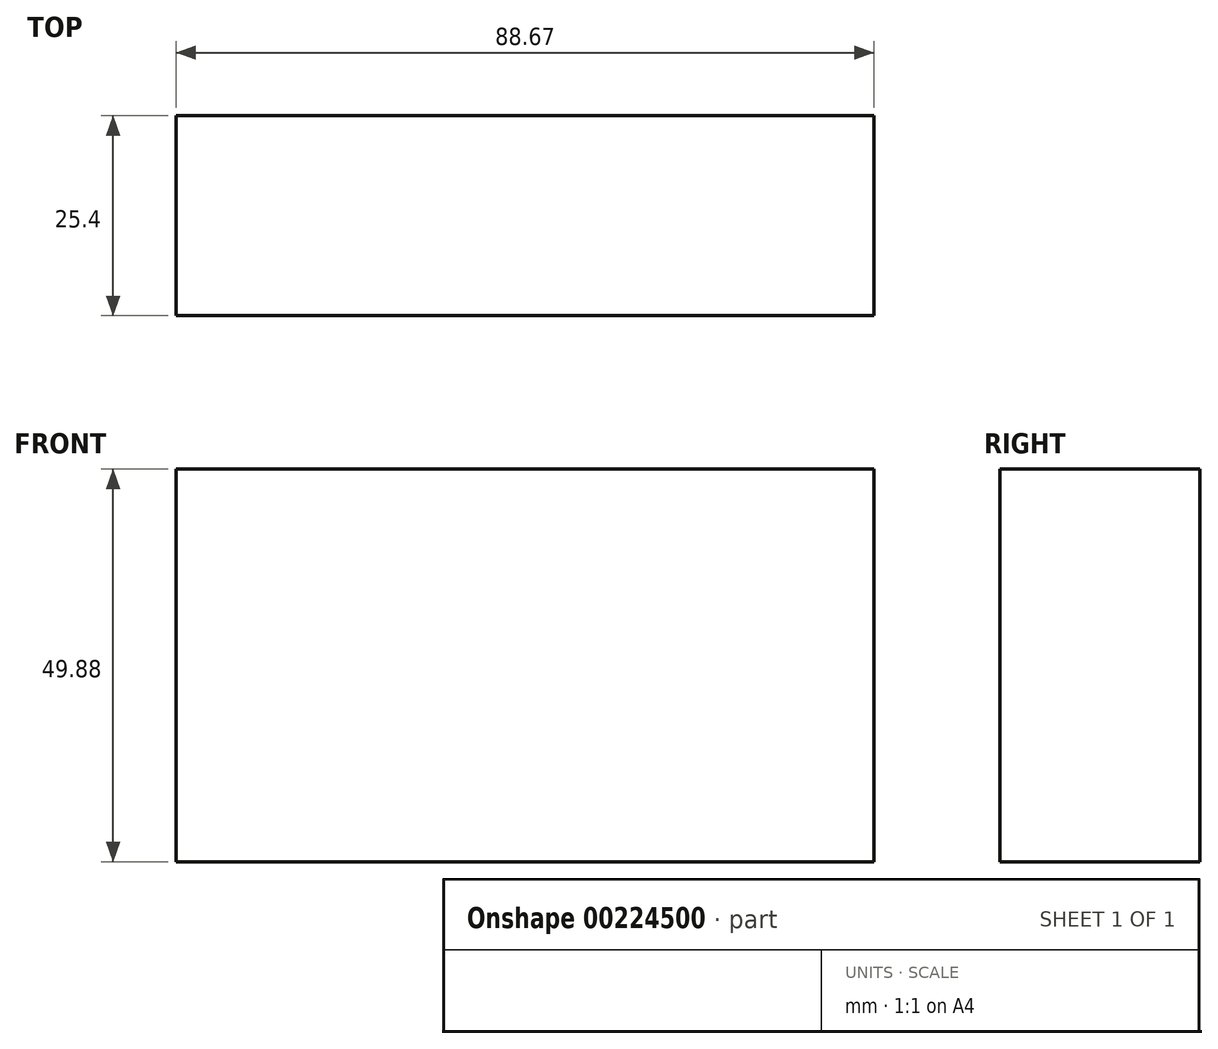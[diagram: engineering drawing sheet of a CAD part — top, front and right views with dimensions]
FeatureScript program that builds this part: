
annotation { "Feature Type Name" : "Feature", "Feature Type Description" : "" }
export const myFeature = defineFeature(function(context is Context, id is Id, definition is map)
    precondition{}
    {
        {
            var Q0;
            Q0=qCreatedBy(makeId("Front.planeOp"),FACE);
            var sketch = newSketch(context, id + "F0", { "sketchPlane" : qUnion([Q0])});
            skLineSegment(sketch, "E0.bottom", {"start": v(-41.33, 25.98) * mm, "end": v(47.34, 25.98) * mm});
            skLineSegment(sketch, "E0.top", {"start": v(-41.33, -23.9) * mm, "end": v(47.34, -23.9) * mm});
            skLineSegment(sketch, "E0.left", {"start": v(-41.33, 25.98) * mm, "end": v(-41.33, -23.9) * mm});
            skLineSegment(sketch, "E0.right", {"start": v(47.34, 25.98) * mm, "end": v(47.34, -23.9) * mm});
            skSolve(sketch);
        }
        {
            var Q0;
            Q0=makeQuery(id+"F0.imprint","IMPRINT",FACE,{"disambiguationData":[TD([[makeQuery(id+"F0.imprint","IMPRINT",EDGE,{"derivedFrom":sQuery(id+"F0.wireOp",EDGE,"E0.bottom")}),-1.0]])]});
            extrude(context, id + "F1", {"entities" : qUnion([Q0]), "depth" : 25.4 * mm});
        }
    });
